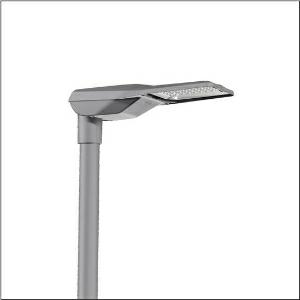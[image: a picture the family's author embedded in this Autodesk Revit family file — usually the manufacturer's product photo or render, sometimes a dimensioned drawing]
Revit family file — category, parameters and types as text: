
# Revit family: streetlight_sl_21_iq_mini___st0_8a_5xe2c41d08jb_a90a
name_source: partatom
category: Lighting Fixtures
units: mm (PartAtom-declared; Revit-internal decimal feet)

## family parameters
Cut with Voids When Loaded = No
Host = Face
Light Source = No
Part Type = Normal
Room Calculation Point = No
Round Connector Dimension = Use Diameter
Shared = No

## types (1)
- --- (1 x LED, 11290 lm, 71.6 W, 4000K)
    Apparent Load = 72 VA
    CIE Flux Codes = 41 75 97 100 100
    Color Rendering = 70
    Color Temperature = 4000K
    Default Elevation = 1800 mm
    Description = Streetlight SL 21 iQ mini, mast luminaire, primary light control with lens, of PMMA, primary optical cover: cover, of toughened safety glass, transparent, light distribution: ST0.8a, light emission: direct distribution, primary light characteristic: asymmetric, installation type: post-top, side-entry, LED, High Power LED, rated luminous flux: 11.290lm, luminous efficacy: 158lm/W, light colour: 740, colour temperature: 4000K, control gear: iQ-Comfort, control: Auto-Match, Temp-Guard, Lumen-Switch, Night-Set, Smart-Wire, Light-Fading, Desk-Remote (wireless, voltage-free reading and setting of iQ features in the workshop via application-optimized NFC function/RFID function), optimised constant luminous flux control (CLO 2.0), pre-setting: linear dimming characteristic, mains connection: 220..240V, AC, 50/60Hz, start of lifetime: 72W, end of service life: 75W, reduction: 33W, luminaire housing, of diecast aluminium, powder-coated, SITECO metallic grey (DB 702S), corrosivity category C5 high according to DIN EN ISO 12944, please order mast flange separately, inclination adjustable: 0°, 5°, 10°, 15°, sealing non-destructively replaceable, multi-level sealing system, length: 628mm, width: 235mm, height: 110mm, mast flange for spigot size: 42mm (side-entry): 5XC10008XM4, 60/48mm (side-entry/post-top): 5XC10108XM2, 76/60mm (side-entry/post-top): 5XC10108XM1, mounting height: 4..8m, protection rating (complete): IP66, insulation class (complete): insulation class II (safety insulation), certification: CE, ENEC, ENEC+, VDE, impact resistance: IK10, permissible operating ambient temperature for outdoor applications: -40..+50°C, standard-compliant lighting for roads and squares, packaging unit: 1 piece

Light Distribution: ST0.8a
    Height = 110 mm
    Lamp = 1 x LED
    Lamp Light Flux = 11290 lm
    Lamp Power = 71.6 W
    Lamp count = 1
    Length = 625 mm
    Luminous efficacy = 158 lm/W
    Manufacturer = Siteco
    ModVariant = No
    Model = 5XE2C41D08JB
    Number of Poles = 1
    OnlyDefault = Yes
    Power Factor = 1
    Product Name = Streetlight SL 21 iQ mini | ST0.8a
    Product group = mast luminaire | pylon top
    ProductGroupID = 6100
    Protection Class = Protection class II
    Protection Degree = IP 66
    RLX_Detail_Level = 1
    RLX_Emergency_Light_Flux = 0 lm
    RLX_Emergency_Type = 0
    RLX_Emergency_Type_DB = No
    RlxData = <blob elided: 26365 chars, md5=973c07ee>
    Socket = socket
    Standby Power = 0 W
    System Light Flux = 11290 lm
    System Power = 72 W
    Type Comments = factory setting: luminous flux: 100 % | dim-lin: 254 | 746 mA
    Type Image = l_1003519.jpg
    URL = http://relux.com
    VarID = @adj_168707
    Voltage = 0 V
    Weight = 0.00 kg
    Width = 234 mm

## geometry (parser evidence)
native form markers: Blend x4, Sweep x9
no freeform markers — native parametric forms only
